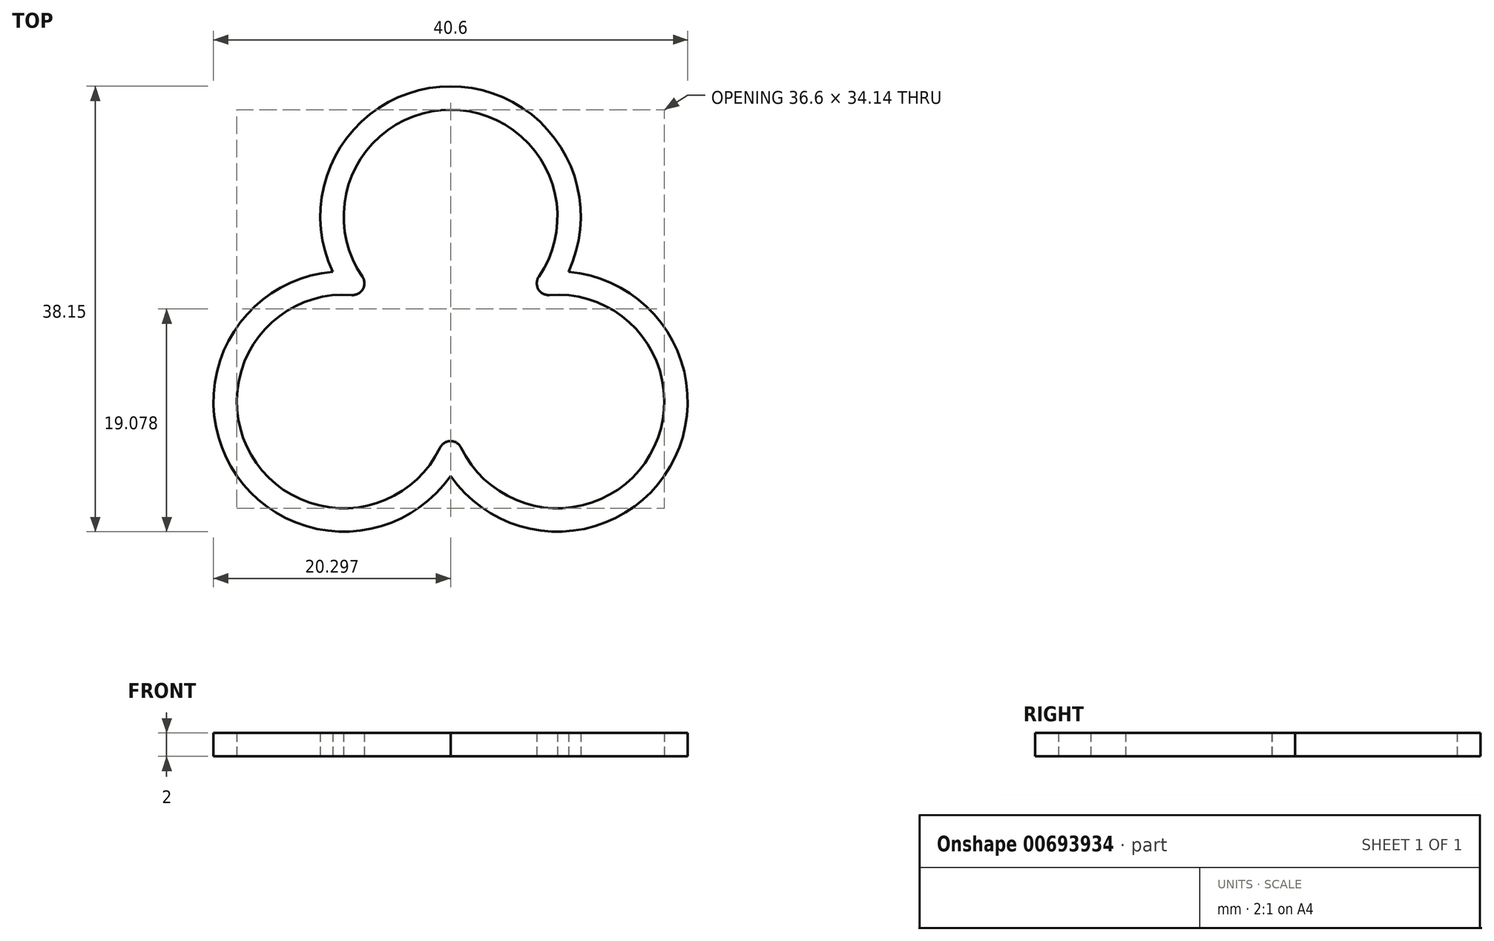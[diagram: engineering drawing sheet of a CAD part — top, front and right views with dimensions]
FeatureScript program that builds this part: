
annotation { "Feature Type Name" : "Feature", "Feature Type Description" : "" }
export const myFeature = defineFeature(function(context is Context, id is Id, definition is map)
    precondition{}
    {
        {
            var Q0;
            Q0=qCreatedBy(makeId("Top.planeOp"),FACE);
            var sketch = newSketch(context, id + "F0", { "sketchPlane" : qUnion([Q0])});
            skArc(sketch, "E0", {"start": v(-29.35, 9.12) * mm, "mid": v(-37.97, -4.57) * mm, "end": v(-21.8, -3.96) * mm});
            skArc(sketch, "E1", {"start": v(-20, -3.96) * mm, "mid": v(-3.82, -4.57) * mm, "end": v(-12.44, 9.12) * mm});
            skArc(sketch, "E2", {"start": v(-13.34, 10.69) * mm, "mid": v(-20.9, 25) * mm, "end": v(-28.45, 10.69) * mm});
            skArc(sketch, "E3.0", {"start": v(-10.8, 11.11) * mm, "mid": v(-20.9, 27) * mm, "end": v(-30.99, 11.11) * mm});
            skArc(sketch, "E3.1", {"start": v(-20.9, -6.37) * mm, "mid": v(-2.09, -5.57) * mm, "end": v(-10.8, 11.11) * mm});
            skArc(sketch, "E3.2", {"start": v(-30.99, 11.11) * mm, "mid": v(-39.7, -5.57) * mm, "end": v(-20.9, -6.37) * mm});
            skPoint(sketch, "E4.visualSharp", {"position": v(-25.47, 7.92) * mm});
            skArc(sketch, "E4.filletArc", {"start": v(-29.35, 9.12) * mm, "mid": v(-28.4, 9.62) * mm, "end": v(-28.45, 10.69) * mm});
            skPoint(sketch, "E5.visualSharp", {"position": v(-16.32, 7.92) * mm});
            skArc(sketch, "E5.filletArc", {"start": v(-13.34, 10.69) * mm, "mid": v(-13.38, 9.62) * mm, "end": v(-12.44, 9.12) * mm});
            skPoint(sketch, "E6.visualSharp", {"position": v(-20.9, 0) * mm});
            skArc(sketch, "E6.filletArc", {"start": v(-20, -3.96) * mm, "mid": v(-20.9, -3.4) * mm, "end": v(-21.8, -3.96) * mm});
            skSolve(sketch);
        }
        {
            var Q0;
            Q0 = qSketchRegion(id + "F0", true);
            extrude(context, id + "F1", {"entities" : qUnion([Q0]), "depth" : 2 * mm, "offsetDistance" : 25 * mm});
        }
    });
